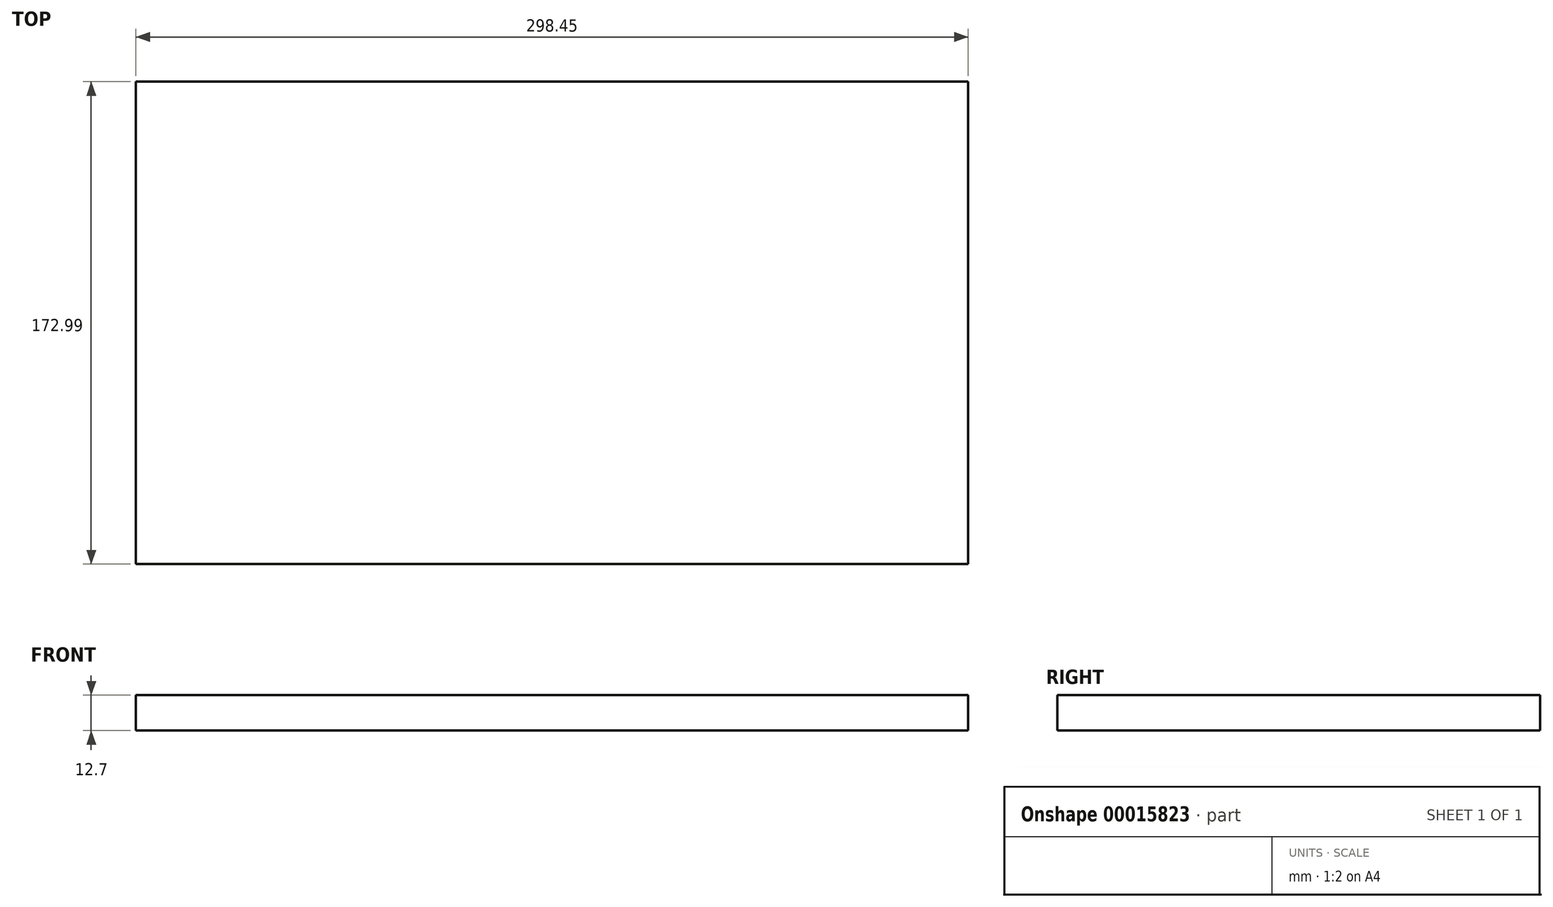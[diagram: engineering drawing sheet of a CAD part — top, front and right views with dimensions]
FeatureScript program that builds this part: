
annotation { "Feature Type Name" : "Feature", "Feature Type Description" : "" }
export const myFeature = defineFeature(function(context is Context, id is Id, definition is map)
    precondition{}
    {
        {
            var Q0;
            Q0=qCreatedBy(makeId("Top.planeOp"),FACE);
            var sketch = newSketch(context, id + "F0", { "sketchPlane" : qUnion([Q0])});
            skLineSegment(sketch, "E0.bottom", {"start": v(0, 0) * mm, "end": v(298.45, 0) * mm});
            skLineSegment(sketch, "E0.top", {"start": v(0, -173) * mm, "end": v(298.45, -173) * mm});
            skLineSegment(sketch, "E0.left", {"start": v(0, 0) * mm, "end": v(0, -173) * mm});
            skLineSegment(sketch, "E0.right", {"start": v(298.45, 0) * mm, "end": v(298.45, -173) * mm});
            skSolve(sketch);
        }
        {
            var Q0;
            Q0 = qSketchRegion(id + "F0", true);
            extrude(context, id + "F1", {"entities" : qUnion([Q0]), "depth" : 12.7 * mm});
        }
    });
